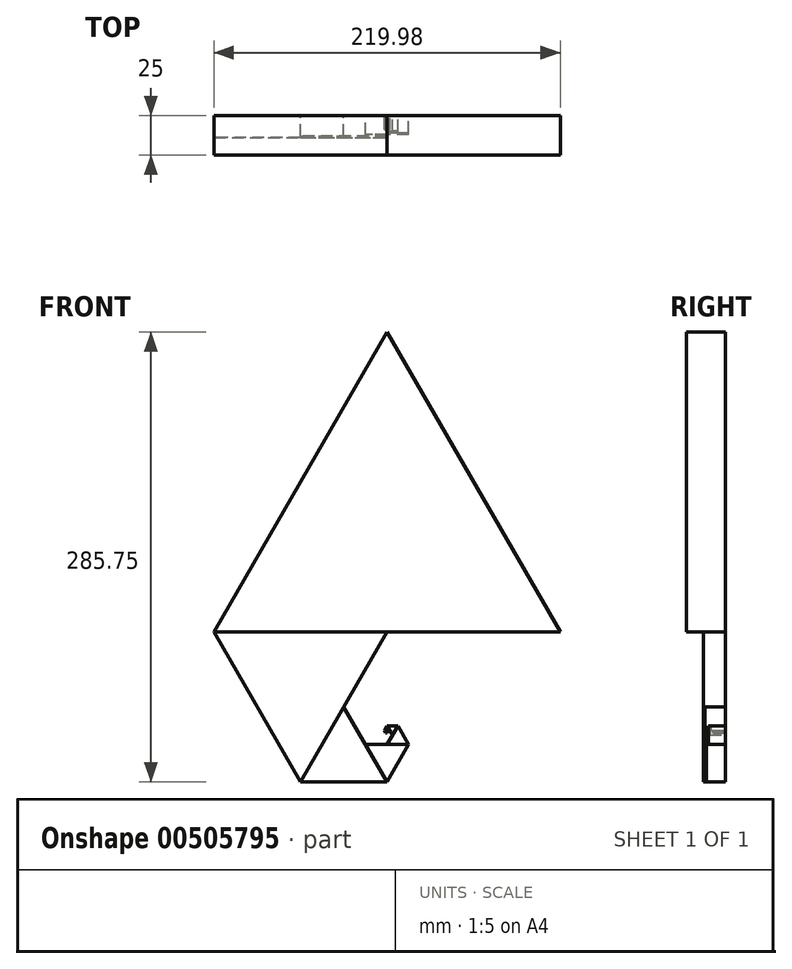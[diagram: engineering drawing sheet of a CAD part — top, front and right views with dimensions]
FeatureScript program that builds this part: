
annotation { "Feature Type Name" : "Feature", "Feature Type Description" : "" }
export const myFeature = defineFeature(function(context is Context, id is Id, definition is map)
    precondition{}
    {
        {
            var Q0;
            Q0=qCreatedBy(makeId("Front.planeOp"),FACE);
            var sketch = newSketch(context, id + "F0", { "sketchPlane" : qUnion([Q0])});
            skCircle(sketch, "E0.cCircle", {"center": v(0, 0) * mm, "radius": 254 * mm, "construction": true});
            skLineSegment(sketch, "E0.0", {"start": v(0, 254) * mm, "end": v(219.97, -127) * mm});
            skLineSegment(sketch, "E0.1", {"start": v(219.97, -127) * mm, "end": v(-219.97, -127) * mm});
            skLineSegment(sketch, "E0.2", {"start": v(-219.97, -127) * mm, "end": v(0, 254) * mm});
            skCircle(sketch, "E1.cCircle", {"center": v(0, 0) * mm, "radius": 127 * mm, "construction": true});
            skLineSegment(sketch, "E1.0", {"start": v(109.99, 63.5) * mm, "end": v(0, -127) * mm});
            skLineSegment(sketch, "E1.1", {"start": v(0, -127) * mm, "end": v(-109.99, 63.5) * mm});
            skLineSegment(sketch, "E1.2", {"start": v(-109.99, 63.5) * mm, "end": v(109.99, 63.5) * mm});
            skCircle(sketch, "E2.cCircle", {"center": v(0, 0) * mm, "radius": 63.5 * mm, "construction": true});
            skLineSegment(sketch, "E2.0", {"start": v(0, 63.5) * mm, "end": v(55, -31.75) * mm});
            skLineSegment(sketch, "E2.1", {"start": v(55, -31.75) * mm, "end": v(-55, -31.75) * mm});
            skLineSegment(sketch, "E2.2", {"start": v(-55, -31.75) * mm, "end": v(0, 63.5) * mm});
            skCircle(sketch, "E3.cCircle", {"center": v(0, 0) * mm, "radius": 31.75 * mm, "construction": true});
            skLineSegment(sketch, "E3.0", {"start": v(27.5, 15.88) * mm, "end": v(0, -31.75) * mm});
            skLineSegment(sketch, "E3.1", {"start": v(0, -31.75) * mm, "end": v(-27.5, 15.87) * mm});
            skLineSegment(sketch, "E3.2", {"start": v(-27.5, 15.87) * mm, "end": v(27.5, 15.88) * mm});
            skCircle(sketch, "E4.cCircle", {"center": v(0, 0) * mm, "radius": 15.87 * mm, "construction": true});
            skLineSegment(sketch, "E4.0", {"start": v(0, 15.87) * mm, "end": v(13.75, -7.94) * mm});
            skLineSegment(sketch, "E4.1", {"start": v(13.75, -7.94) * mm, "end": v(-13.75, -7.94) * mm});
            skLineSegment(sketch, "E4.2", {"start": v(-13.75, -7.94) * mm, "end": v(0, 15.87) * mm});
            skCircle(sketch, "E5.cCircle", {"center": v(0, 0) * mm, "radius": 7.94 * mm, "construction": true});
            skLineSegment(sketch, "E5.0", {"start": v(6.87, 3.97) * mm, "end": v(0, -7.94) * mm});
            skLineSegment(sketch, "E5.1", {"start": v(0, -7.94) * mm, "end": v(-6.87, 3.97) * mm});
            skLineSegment(sketch, "E5.2", {"start": v(-6.87, 3.97) * mm, "end": v(6.87, 3.97) * mm});
            skCircle(sketch, "E6.cCircle", {"center": v(0, 0) * mm, "radius": 3.97 * mm, "construction": true});
            skLineSegment(sketch, "E6.0", {"start": v(0, 3.97) * mm, "end": v(3.44, -1.98) * mm});
            skLineSegment(sketch, "E6.1", {"start": v(3.44, -1.98) * mm, "end": v(-3.44, -1.98) * mm});
            skLineSegment(sketch, "E6.2", {"start": v(-3.44, -1.98) * mm, "end": v(0, 3.97) * mm});
            skCircle(sketch, "E7.cCircle", {"center": v(0, 0) * mm, "radius": 1.98 * mm, "construction": true});
            skLineSegment(sketch, "E7.0", {"start": v(1.72, 1) * mm, "end": v(0, -1.98) * mm});
            skLineSegment(sketch, "E7.1", {"start": v(0, -1.98) * mm, "end": v(-1.72, 1) * mm});
            skLineSegment(sketch, "E7.2", {"start": v(-1.72, 1) * mm, "end": v(1.72, 1) * mm});
            skCircle(sketch, "E8.cCircle", {"center": v(0, 0) * mm, "radius": 1 * mm, "construction": true});
            skLineSegment(sketch, "E8.0", {"start": v(0, 1) * mm, "end": v(0.86, -0.5) * mm});
            skLineSegment(sketch, "E8.1", {"start": v(0.86, -0.5) * mm, "end": v(-0.86, -0.5) * mm});
            skLineSegment(sketch, "E8.2", {"start": v(-0.86, -0.5) * mm, "end": v(0, 1) * mm});
            skCircle(sketch, "E9.cCircle", {"center": v(0, 0) * mm, "radius": 0.5 * mm, "construction": true});
            skLineSegment(sketch, "E9.0", {"start": v(0.43, 0.25) * mm, "end": v(0, -0.5) * mm});
            skLineSegment(sketch, "E9.1", {"start": v(0, -0.5) * mm, "end": v(-0.43, 0.25) * mm});
            skLineSegment(sketch, "E9.2", {"start": v(-0.43, 0.25) * mm, "end": v(0.43, 0.25) * mm});
            skCircle(sketch, "E10.cCircle", {"center": v(0, 0) * mm, "radius": 0.25 * mm, "construction": true});
            skLineSegment(sketch, "E10.0", {"start": v(0, 0.25) * mm, "end": v(0.21, -0.12) * mm});
            skLineSegment(sketch, "E10.1", {"start": v(0.21, -0.12) * mm, "end": v(-0.21, -0.12) * mm});
            skLineSegment(sketch, "E10.2", {"start": v(-0.21, -0.12) * mm, "end": v(0, 0.25) * mm});
            skCircle(sketch, "E11.cCircle", {"center": v(0, 0) * mm, "radius": 0.12 * mm, "construction": true});
            skLineSegment(sketch, "E11.0", {"start": v(0.1, 0.06) * mm, "end": v(0, -0.12) * mm});
            skLineSegment(sketch, "E11.1", {"start": v(0, -0.12) * mm, "end": v(-0.1, 0.06) * mm});
            skLineSegment(sketch, "E11.2", {"start": v(-0.1, 0.06) * mm, "end": v(0.1, 0.06) * mm});
            skCircle(sketch, "E12.cCircle", {"center": v(0, 0) * mm, "radius": 0.06 * mm, "construction": true});
            skLineSegment(sketch, "E12.0", {"start": v(0, 0.06) * mm, "end": v(0.05, -0.03) * mm});
            skLineSegment(sketch, "E12.1", {"start": v(0.05, -0.03) * mm, "end": v(-0.05, -0.03) * mm});
            skLineSegment(sketch, "E12.2", {"start": v(-0.05, -0.03) * mm, "end": v(0, 0.06) * mm});
            skCircle(sketch, "E13.cCircle", {"center": v(0, 0) * mm, "radius": 0.03 * mm, "construction": true});
            skLineSegment(sketch, "E13.0", {"start": v(0.03, 0.02) * mm, "end": v(0, -0.03) * mm});
            skLineSegment(sketch, "E13.1", {"start": v(0, -0.03) * mm, "end": v(-0.03, 0.02) * mm});
            skLineSegment(sketch, "E13.2", {"start": v(-0.03, 0.02) * mm, "end": v(0.03, 0.02) * mm});
            skCircle(sketch, "E14.cCircle", {"center": v(0, 0) * mm, "radius": 0.02 * mm, "construction": true});
            skLineSegment(sketch, "E14.0", {"start": v(0, 0.02) * mm, "end": v(0.01, 0) * mm});
            skLineSegment(sketch, "E14.1", {"start": v(0.01, 0) * mm, "end": v(-0.01, 0) * mm});
            skLineSegment(sketch, "E14.2", {"start": v(-0.01, 0) * mm, "end": v(0, 0.02) * mm});
            skSolve(sketch);
        }
        {
            var Q0;
            Q0=makeQuery(id+"F0.imprint","IMPRINT",FACE,{"disambiguationData":[TD([[makeQuery(id+"F0.imprint","IMPRINT",EDGE,{"derivedFrom":sQuery(id+"F0.wireOp",EDGE,"E14.0")}),-1.0]])]});
            extrude(context, id + "F1", {"entities" : qUnion([Q0]), "depth" : 1 * mm, "offsetDistance" : 25 * mm});
        }
        {
            var Q0;
            {var subQ3=sQuery(id+"F0.wireOp",EDGE,"E14.2");Q0=makeQuery(id+"F0.imprint","IMPRINT",FACE,{"disambiguationData":[TD([[makeQuery(id+"F0.imprint","IMPRINT",EDGE,{"derivedFrom":subQ3}),1.0]])]});}
            extrude(context, id + "F2", {"entities" : qUnion([Q0]), "operationType" : NewBodyOperationType.ADD, "depth" : 2 * mm, "offsetDistance" : 25 * mm});
        }
        {
            var Q0;
            {var subQ0=sQuery(id+"F0.wireOp",EDGE,"E12.2");var subQ1=sQuery(id+"F0.wireOp",EDGE,"E12.0");var subQ2=makeQuery(id+"F0.imprint","INTERSECT",VERTEX,{"derivedFrom":[sQuery(id+"F0.wireOp",EDGE,"E11.2"),subQ1,subQ0]});Q0=makeQuery(id+"F0.imprint","IMPRINT",FACE,{"disambiguationData":[TD([[makeQuery(id+"F0.imprint","IMPRINT",EDGE,{"disambiguationData":[TD([[subQ2,-1.0]])],"derivedFrom":subQ1}),-1.0]])]});}
            extrude(context, id + "F3", {"entities" : qUnion([Q0]), "operationType" : NewBodyOperationType.ADD, "depth" : 3 * mm, "offsetDistance" : 25 * mm});
        }
        {
            var Q0;
            {var subQ0=sQuery(id+"F0.wireOp",EDGE,"E11.2");var subQ1=sQuery(id+"F0.wireOp",EDGE,"E11.0");var subQ2=makeQuery(id+"F0.imprint","INTERSECT",VERTEX,{"derivedFrom":[sQuery(id+"F0.wireOp",EDGE,"E10.0"),subQ1,subQ0]});Q0=makeQuery(id+"F0.imprint","IMPRINT",FACE,{"disambiguationData":[TD([[makeQuery(id+"F0.imprint","IMPRINT",EDGE,{"disambiguationData":[TD([[subQ2,-1.0]])],"derivedFrom":subQ1}),-1.0]])]});}
            extrude(context, id + "F4", {"entities" : qUnion([Q0]), "operationType" : NewBodyOperationType.ADD, "depth" : 4 * mm, "offsetDistance" : 25 * mm});
        }
        {
            var Q0;
            {var subQ0=sQuery(id+"F0.wireOp",EDGE,"E10.1");var subQ1=sQuery(id+"F0.wireOp",EDGE,"E10.0");var subQ2=makeQuery(id+"F0.imprint","INTERSECT",VERTEX,{"derivedFrom":[sQuery(id+"F0.wireOp",EDGE,"E9.0"),subQ1,subQ0]});Q0=makeQuery(id+"F0.imprint","IMPRINT",FACE,{"disambiguationData":[TD([[makeQuery(id+"F0.imprint","IMPRINT",EDGE,{"disambiguationData":[TD([[subQ2,1.0]])],"derivedFrom":subQ1}),-1.0]])]});}
            extrude(context, id + "F5", {"entities" : qUnion([Q0]), "operationType" : NewBodyOperationType.ADD, "depth" : 5 * mm, "offsetDistance" : 25 * mm});
        }
        {
            var Q0;
            {var subQ0=sQuery(id+"F0.wireOp",EDGE,"E9.1");var subQ1=sQuery(id+"F0.wireOp",EDGE,"E9.0");var subQ2=makeQuery(id+"F0.imprint","INTERSECT",VERTEX,{"derivedFrom":[sQuery(id+"F0.wireOp",EDGE,"E8.1"),subQ1,subQ0]});Q0=makeQuery(id+"F0.imprint","IMPRINT",FACE,{"disambiguationData":[TD([[makeQuery(id+"F0.imprint","IMPRINT",EDGE,{"disambiguationData":[TD([[subQ2,1.0]])],"derivedFrom":subQ1}),-1.0]])]});}
            extrude(context, id + "F6", {"entities" : qUnion([Q0]), "operationType" : NewBodyOperationType.ADD, "depth" : 6 * mm, "offsetDistance" : 25 * mm});
        }
        {
            var Q0;
            {var subQ0=sQuery(id+"F0.wireOp",EDGE,"E8.2");var subQ1=sQuery(id+"F0.wireOp",EDGE,"E8.1");var subQ2=makeQuery(id+"F0.imprint","INTERSECT",VERTEX,{"derivedFrom":[sQuery(id+"F0.wireOp",EDGE,"E7.1"),subQ1,subQ0]});Q0=makeQuery(id+"F0.imprint","IMPRINT",FACE,{"disambiguationData":[TD([[makeQuery(id+"F0.imprint","IMPRINT",EDGE,{"disambiguationData":[TD([[subQ2,1.0]])],"derivedFrom":subQ1}),-1.0]])]});}
            extrude(context, id + "F7", {"entities" : qUnion([Q0]), "operationType" : NewBodyOperationType.ADD, "depth" : 7 * mm, "offsetDistance" : 25 * mm});
        }
        {
            var Q0;
            {var subQ0=sQuery(id+"F0.wireOp",EDGE,"E7.2");var subQ1=sQuery(id+"F0.wireOp",EDGE,"E7.1");var subQ2=makeQuery(id+"F0.imprint","INTERSECT",VERTEX,{"derivedFrom":[sQuery(id+"F0.wireOp",EDGE,"E6.2"),subQ1,subQ0]});Q0=makeQuery(id+"F0.imprint","IMPRINT",FACE,{"disambiguationData":[TD([[makeQuery(id+"F0.imprint","IMPRINT",EDGE,{"disambiguationData":[TD([[subQ2,1.0]])],"derivedFrom":subQ1}),-1.0]])]});}
            extrude(context, id + "F8", {"entities" : qUnion([Q0]), "operationType" : NewBodyOperationType.ADD, "depth" : 8 * mm, "offsetDistance" : 25 * mm});
        }
        {
            var Q0;
            {var subQ0=sQuery(id+"F0.wireOp",EDGE,"E6.2");var subQ1=sQuery(id+"F0.wireOp",EDGE,"E6.0");var subQ2=makeQuery(id+"F0.imprint","INTERSECT",VERTEX,{"derivedFrom":[sQuery(id+"F0.wireOp",EDGE,"E5.2"),subQ1,subQ0]});Q0=makeQuery(id+"F0.imprint","IMPRINT",FACE,{"disambiguationData":[TD([[makeQuery(id+"F0.imprint","IMPRINT",EDGE,{"disambiguationData":[TD([[subQ2,-1.0]])],"derivedFrom":subQ1}),-1.0]])]});}
            extrude(context, id + "F9", {"entities" : qUnion([Q0]), "operationType" : NewBodyOperationType.ADD, "depth" : 9 * mm, "offsetDistance" : 25 * mm});
        }
        {
            var Q0;
            {var subQ0=sQuery(id+"F0.wireOp",EDGE,"E5.2");var subQ1=sQuery(id+"F0.wireOp",EDGE,"E5.0");var subQ2=makeQuery(id+"F0.imprint","INTERSECT",VERTEX,{"derivedFrom":[sQuery(id+"F0.wireOp",EDGE,"E4.0"),subQ1,subQ0]});Q0=makeQuery(id+"F0.imprint","IMPRINT",FACE,{"disambiguationData":[TD([[makeQuery(id+"F0.imprint","IMPRINT",EDGE,{"disambiguationData":[TD([[subQ2,-1.0]])],"derivedFrom":subQ1}),-1.0]])]});}
            extrude(context, id + "F10", {"entities" : qUnion([Q0]), "operationType" : NewBodyOperationType.ADD, "depth" : 10 * mm, "offsetDistance" : 25 * mm});
        }
        {
            var Q0;
            {var subQ0=sQuery(id+"F0.wireOp",EDGE,"E4.1");var subQ1=sQuery(id+"F0.wireOp",EDGE,"E4.0");var subQ2=makeQuery(id+"F0.imprint","INTERSECT",VERTEX,{"derivedFrom":[sQuery(id+"F0.wireOp",EDGE,"E3.0"),subQ1,subQ0]});Q0=makeQuery(id+"F0.imprint","IMPRINT",FACE,{"disambiguationData":[TD([[makeQuery(id+"F0.imprint","IMPRINT",EDGE,{"disambiguationData":[TD([[subQ2,1.0]])],"derivedFrom":subQ1}),-1.0]])]});}
            extrude(context, id + "F11", {"entities" : qUnion([Q0]), "operationType" : NewBodyOperationType.ADD, "depth" : 11 * mm, "offsetDistance" : 25 * mm});
        }
        {
            var Q0;
            {var subQ0=sQuery(id+"F0.wireOp",EDGE,"E3.1");var subQ1=sQuery(id+"F0.wireOp",EDGE,"E3.0");var subQ2=makeQuery(id+"F0.imprint","INTERSECT",VERTEX,{"derivedFrom":[sQuery(id+"F0.wireOp",EDGE,"E2.1"),subQ1,subQ0]});Q0=makeQuery(id+"F0.imprint","IMPRINT",FACE,{"disambiguationData":[TD([[makeQuery(id+"F0.imprint","IMPRINT",EDGE,{"disambiguationData":[TD([[subQ2,1.0]])],"derivedFrom":subQ1}),-1.0]])]});}
            extrude(context, id + "F12", {"entities" : qUnion([Q0]), "operationType" : NewBodyOperationType.ADD, "depth" : 12 * mm, "offsetDistance" : 25 * mm});
        }
        {
            var Q0;
            {var subQ0=sQuery(id+"F0.wireOp",EDGE,"E2.2");var subQ1=sQuery(id+"F0.wireOp",EDGE,"E2.1");var subQ2=makeQuery(id+"F0.imprint","INTERSECT",VERTEX,{"derivedFrom":[sQuery(id+"F0.wireOp",EDGE,"E1.1"),subQ1,subQ0]});Q0=makeQuery(id+"F0.imprint","IMPRINT",FACE,{"disambiguationData":[TD([[makeQuery(id+"F0.imprint","IMPRINT",EDGE,{"disambiguationData":[TD([[subQ2,1.0]])],"derivedFrom":subQ1}),-1.0]])]});}
            extrude(context, id + "F13", {"entities" : qUnion([Q0]), "operationType" : NewBodyOperationType.ADD, "depth" : 13 * mm, "offsetDistance" : 25 * mm});
        }
        {
            var Q0;
            {var subQ0=sQuery(id+"F0.wireOp",EDGE,"E1.2");var subQ1=sQuery(id+"F0.wireOp",EDGE,"E1.1");var subQ2=makeQuery(id+"F0.imprint","INTERSECT",VERTEX,{"derivedFrom":[sQuery(id+"F0.wireOp",EDGE,"E0.2"),subQ1,subQ0]});Q0=makeQuery(id+"F0.imprint","IMPRINT",FACE,{"disambiguationData":[TD([[makeQuery(id+"F0.imprint","IMPRINT",EDGE,{"disambiguationData":[TD([[subQ2,1.0]])],"derivedFrom":subQ1}),-1.0]])]});}
            extrude(context, id + "F14", {"entities" : qUnion([Q0]), "operationType" : NewBodyOperationType.ADD, "depth" : 14 * mm, "offsetDistance" : 25 * mm});
        }
        {
            var Q0;
            {var subQ0=sQuery(id+"F0.wireOp",EDGE,"E0.2");var subQ1=sQuery(id+"F0.wireOp",EDGE,"E0.0");var subQ2=makeQuery(id+"F0.imprint","INTERSECT",VERTEX,{"derivedFrom":[subQ1,subQ0]});Q0=makeQuery(id+"F0.imprint","IMPRINT",FACE,{"disambiguationData":[TD([[makeQuery(id+"F0.imprint","IMPRINT",EDGE,{"disambiguationData":[TD([[subQ2,-1.0]])],"derivedFrom":subQ1}),-1.0]])]});}
            extrude(context, id + "F15", {"entities" : qUnion([Q0]), "operationType" : NewBodyOperationType.ADD, "depth" : 25 * mm, "offsetDistance" : 25 * mm});
        }
    });
